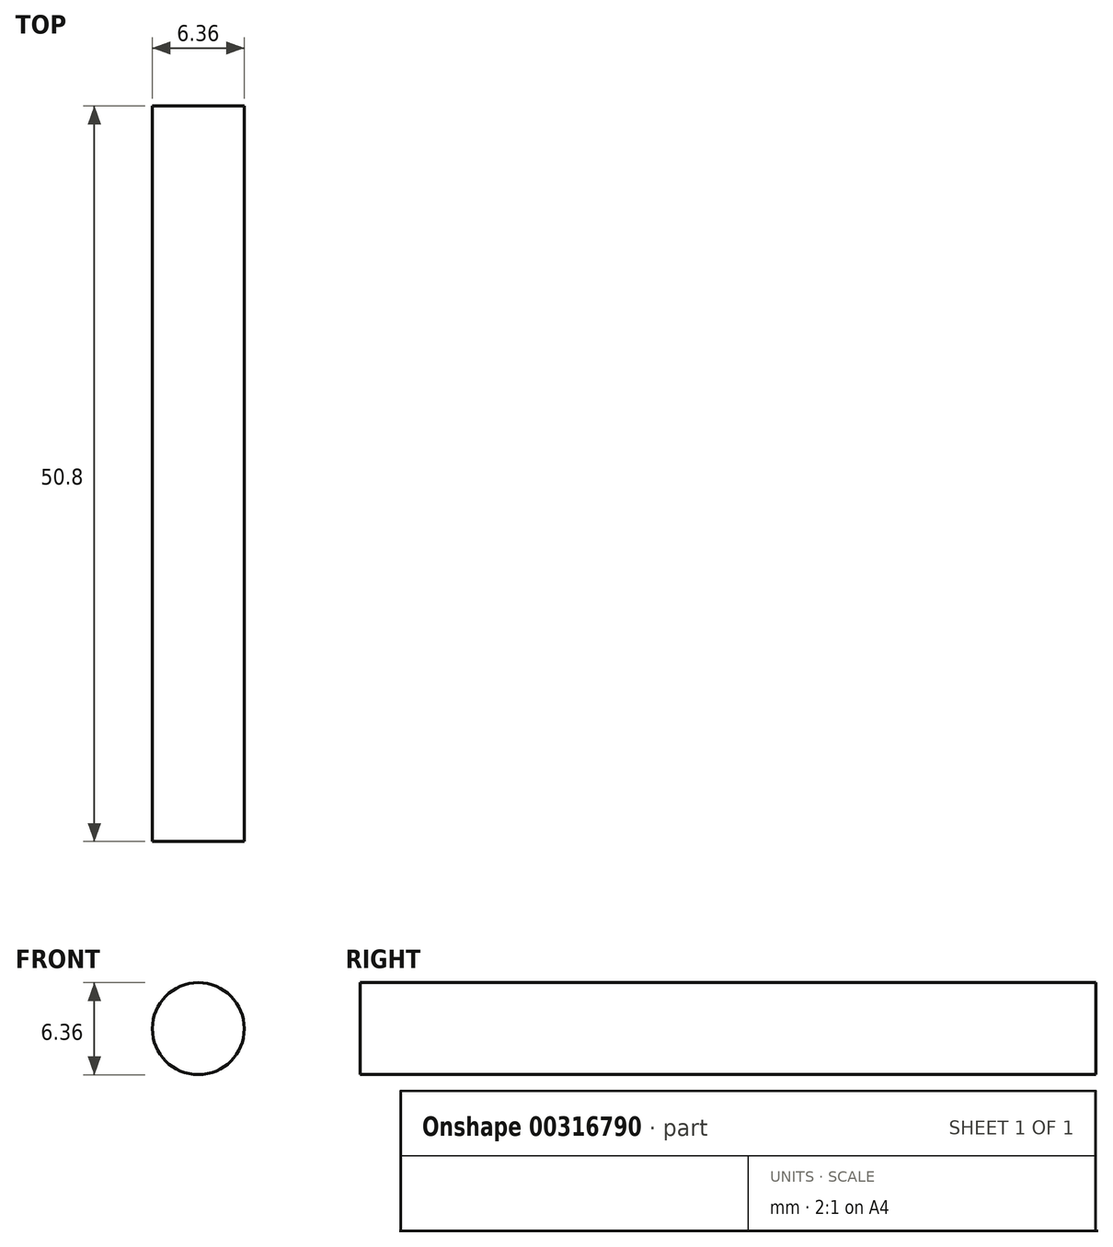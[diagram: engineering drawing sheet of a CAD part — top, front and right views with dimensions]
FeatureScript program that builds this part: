
annotation { "Feature Type Name" : "Feature", "Feature Type Description" : "" }
export const myFeature = defineFeature(function(context is Context, id is Id, definition is map)
    precondition{}
    {
        {
            var Q0;
            Q0=qCreatedBy(makeId("Front.planeOp"),FACE);
            var sketch = newSketch(context, id + "F0", { "sketchPlane" : qUnion([Q0])});
            skCircle(sketch, "E0", {"center": v(0, 0) * mm, "radius": 3.18 * mm});
            skSolve(sketch);
        }
        {
            var Q0;
            Q0=qSketchRegion(id+"F0",true);
            extrude(context, id + "F1", {"entities" : qUnion([Q0]), "depth" : 50.8 * mm});
        }
    });
